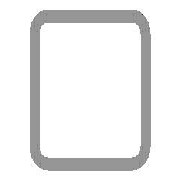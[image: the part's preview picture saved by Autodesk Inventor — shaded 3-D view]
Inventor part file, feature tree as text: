
AUTODESK INVENTOR PART (.ipt)
format: ipt  version: 2025.3 (Build 293356000, 356)  size: 142,336 bytes
history: native  units: mm (DEFAULTED — no unit token found)
features: other x4, plane x2, split x1, sketch x1
ambient origin geometry x8: Origin, YZ Plane, XZ Plane, XY Plane, X Axis, Y Axis, Z Axis, Center Point
bodies: Solid1 (feature_tree), Body (feature_tree)
feature tree (8):
  parser-record x1  (decoder bookkeeping rows leaked as tree rows — omitted from the tree; the rows remain in map.json)
  other  "Driven Length"
  other  "Start Plane"
  other  "End Plane"
  plane  "Work Plane4"
  split  "Split1"
  sketch  "Sketch3"  dims[d3=2639.340203mm d4=0.0mm d7=6.0mm d9=80.0mm d11=80.0mm d12=3.0mm d13=160.659797mm d14=2800.0mm d15=40.0mm d16=40.0mm d17=90.0deg d18=2639.340203mm]
  plane  "Work Plane3"
